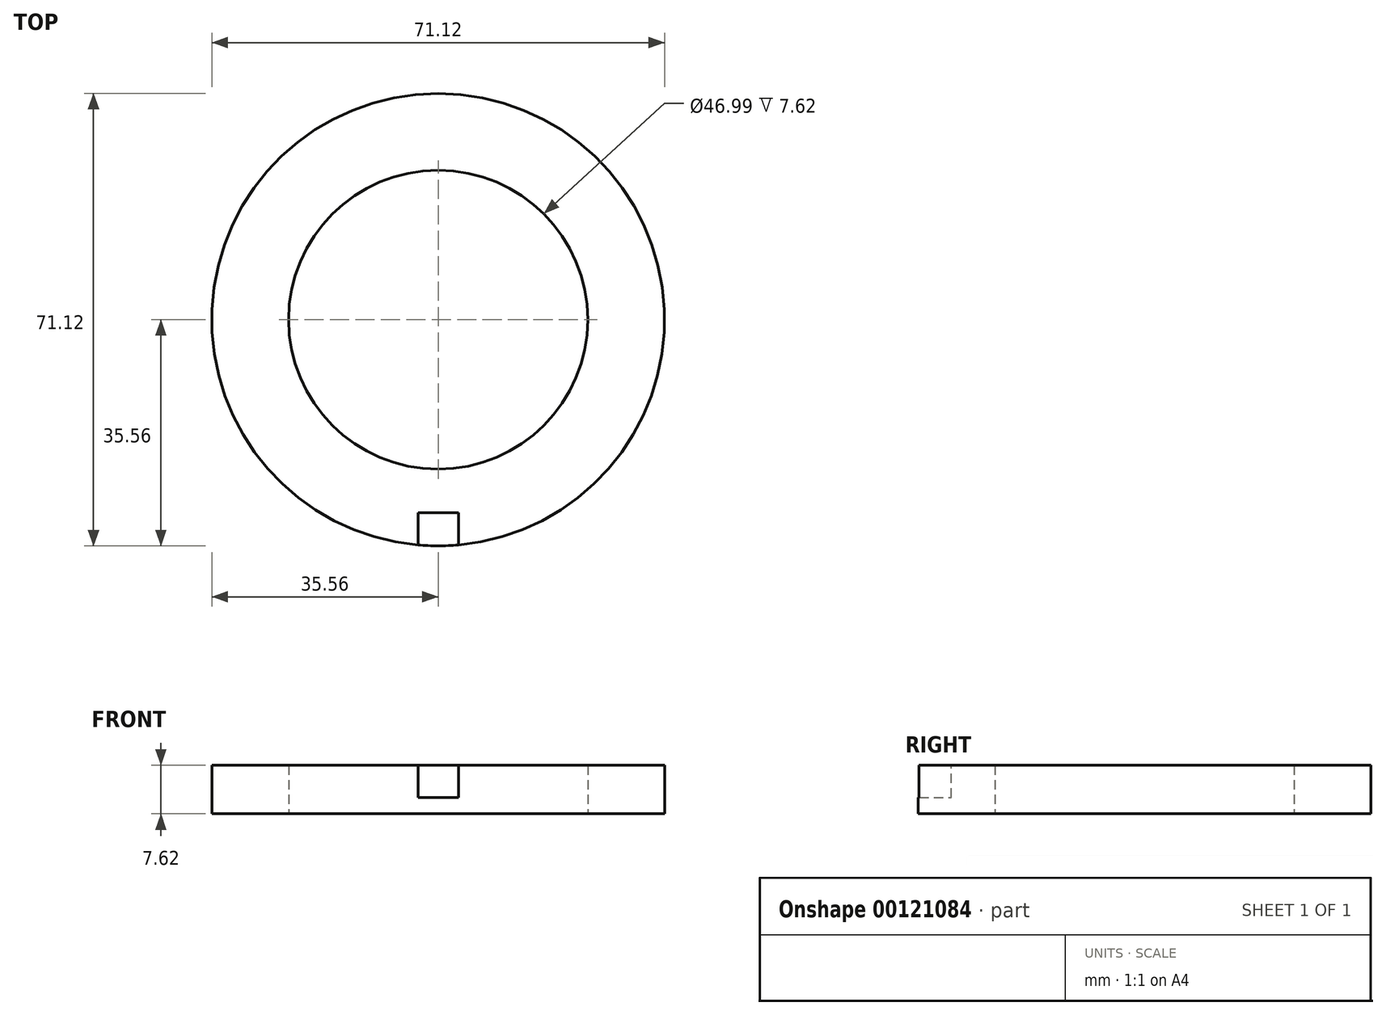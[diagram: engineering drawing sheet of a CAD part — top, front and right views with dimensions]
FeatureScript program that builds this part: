
annotation { "Feature Type Name" : "Feature", "Feature Type Description" : "" }
export const myFeature = defineFeature(function(context is Context, id is Id, definition is map)
    precondition{}
    {
        {
            var Q0;
            Q0=qCreatedBy(makeId("Top.planeOp"),FACE);
            var sketch = newSketch(context, id + "F0", { "sketchPlane" : qUnion([Q0])});
            skCircle(sketch, "E0", {"center": v(0, 0) * mm, "radius": 35.56 * mm});
            skCircle(sketch, "E1.0", {"center": v(0, 0) * mm, "radius": 23.5 * mm});
            skSolve(sketch);
        }
        {
            var Q0;
            Q0=makeQuery(id+"F0.imprint","IMPRINT",FACE,{"disambiguationData":[TD([[makeQuery(id+"F0.imprint","IMPRINT",EDGE,{"derivedFrom":sQuery(id+"F0.wireOp",EDGE,"E0")}),1.0]])]});
            extrude(context, id + "F1", {"entities" : qUnion([Q0]), "depth" : 7.62 * mm});
        }
        {
            var Q0;
            Q0=makeQuery(id+"F1.opExtrude","CAP_FACE",FACE,{"disambiguationData":[OSD([sQuery(id+"F0.wireOp",EDGE,"E0"),sQuery(id+"F0.wireOp",EDGE,"E1.0")])],"isStart":false});
            var sketch = newSketch(context, id + "F2", { "sketchPlane" : qUnion([Q0])});
            skLineSegment(sketch, "E2", {"start": v(-3.17, -35.42) * mm, "end": v(-3.17, -30.34) * mm});
            skLineSegment(sketch, "E3", {"start": v(-3.17, -30.34) * mm, "end": v(3.18, -30.34) * mm});
            skLineSegment(sketch, "E4", {"start": v(3.18, -30.34) * mm, "end": v(3.18, -35.42) * mm});
            skPoint(sketch, "E5", {"position": v(0, -30.34) * mm});
            skSolve(sketch);
        }
        {
            var Q0;
            Q0 = qSketchRegion(id + "F2", true);
            var Q1;
            {var subQ0=sQuery(id+"F2.wireOp",EDGE,"E2");Q1=makeQuery(id+"F2.imprint","IMPRINT",FACE,{"disambiguationData":[TD([[makeQuery(id+"F2.imprint","IMPRINT",EDGE,{"derivedFrom":subQ0}),-1.0]])]});}
            extrude(context, id + "F3", {"entities" : qUnion([Q0, Q1]), "operationType" : NewBodyOperationType.REMOVE, "oppositeDirection" : true, "depth" : 5.08 * mm});
        }
    });
